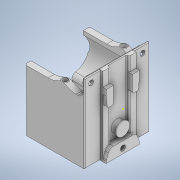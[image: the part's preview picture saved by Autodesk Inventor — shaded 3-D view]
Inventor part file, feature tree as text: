
AUTODESK INVENTOR PART (.ipt)
format: ipt  version: 2022 (Build 260153000, 153)  size: 863,232 bytes
history: native  units: mm
features: reference x27, sketch x24, extrude x22, projected_geometry x19, fillet x13, other x10, chamfer x1
ambient origin geometry x8: Origin, YZ Plane, XZ Plane, XY Plane, X Axis, Y Axis, Z Axis, Center Point
bodies: Body1 (feature_tree)
feature tree (116):
  other  "Твердое тело1"
  extrude  "Выдавливание1"  Depth=34.5mm TaperAngle=0.0deg
  extrude  "Выдавливание2"  Depth=0.5mm
  extrude  "Выдавливание3"  Depth=0.3mm
  extrude  "Выдавливание4"  Depth=5.0mm
  extrude  "Выдавливание5"  Depth=5.0mm
  extrude  "Выдавливание6"  Depth=5.0mm
  extrude  "Выдавливание8"  Depth=15.0mm
  extrude  "Выдавливание9"  Depth=15.0mm
  chamfer  "Фаска1"  Distance=15.0mm
  fillet  "Сопряжение1"  Radius=1.7mm
  extrude  "Выдавливание11"  Depth=2.0mm TaperAngle=0.0deg
  fillet  "Сопряжение4"  Radius=0.8mm
  fillet  "Сопряжение5"  Radius=4.7mm
  sketch  "Эскиз15"
  extrude  "Выдавливание12"  Depth=0.4mm
  sketch  "Эскиз17"
  extrude  "Выдавливание13"  Depth=0.4mm
  extrude  "Выдавливание18"  Depth=200.0mm TaperAngle=0.0deg
  extrude  "Выдавливание19"  Depth=0.5mm TaperAngle=0.0deg
  extrude  "Выдавливание20"  Depth=2.3mm TaperAngle=0.0deg
  extrude  "Выдавливание21"  Depth=10.0mm
  fillet  "Сопряжение13"  Radius=10.0mm
  fillet  "Сопряжение14"  Radius=3.0mm
  fillet  "Сопряжение15"  Radius=4.0mm
  extrude  "Выдавливание22"  Depth=3.0mm
  fillet  "Сопряжение16"  Radius=4.0mm
  extrude  "Выдавливание23"  Depth=2.3mm TaperAngle=0.0deg
  extrude  "Выдавливание24"  Depth=2.3mm TaperAngle=45.0deg
  fillet  "Сопряжение17"  Radius=10.0mm
  extrude  "Выдавливание25"  Depth=30.0mm
  fillet  "Сопряжение19"  Radius=0.8mm
  extrude  "Выдавливание26"  Depth=0.15mm
  fillet  "Сопряжение20"  Radius=3.0mm
  extrude  "Выдавливание27"  Depth=50.0mm TaperAngle=0.0deg
  fillet  "Сопряжение21"  Radius=4.0mm
  fillet  "Сопряжение22"  Radius=4.0mm
  fillet  "Сопряжение23"  Radius=3.2mm
  extrude  "Выдавливание28"  Depth=8.0mm
  sketch  "Эскиз1"
  reference  "Ссылка1"
  reference  "Ссылка2"
  reference  "Ссылка3"
  reference  "Ссылка4"
  reference  "Ссылка5"
  reference  "Ссылка6"
  reference  "Ссылка7"
  reference  "Ссылка8"
  sketch  "Эскиз2"
  projected_geometry  "Спроецированная петля1"
  projected_geometry  "Спроецированная петля2"
  sketch  "Эскиз3"
  reference  "Ссылка9"
  reference  "Ссылка10"
  sketch  "Эскиз4"
  projected_geometry  "Спроецированная петля3"
  reference  "Ссылка11"
  reference  "Ссылка12"
  reference  "Ссылка13"
  reference  "Ссылка14"
  sketch  "Эскиз5"
  reference  "Ссылка15"
  reference  "Ссылка16"
  projected_geometry  "Спроецированная петля4"
  sketch  "Эскиз7"
  projected_geometry  "Спроецированная петля6"
  sketch  "Эскиз11"
  projected_geometry  "Спроецированная петля8"
  sketch  "Эскиз12"
  reference  "Ссылка27"
  sketch  "Эскиз14"
  sketch  "Эскиз16"
  reference  "Ссылка29"
  projected_geometry  "Спроецированная петля10"
  projected_geometry  "Спроецированная петля11"
  projected_geometry  "Спроецированная петля12"
  reference  "Ссылка30"
  reference  "Ссылка31"
  sketch  "Эскиз18"
  projected_geometry  "Спроецированная петля14"
  sketch  "Эскиз23"
  projected_geometry  "Спроецированная петля23"
  sketch  "Эскиз24"
  projected_geometry  "Спроецированная петля24"
  sketch  "Эскиз25"
  sketch  "Эскиз26"
  sketch  "Эскиз27"
  projected_geometry  "Спроецированная петля25"
  sketch  "Эскиз28"
  sketch  "Эскиз29"
  sketch  "Эскиз30"
  reference  "Ссылка32"
  projected_geometry  "Спроецированная петля26"
  projected_geometry  "Спроецированная петля27"
  reference  "Ссылка33"
  projected_geometry  "Спроецированная петля28"
  sketch  "Эскиз31"
  projected_geometry  "Спроецированная петля29"
  projected_geometry  "Спроецированная петля30"
  reference  "Ссылка34"
  reference  "Ссылка35"
  sketch  "Эскиз32"
  reference  "Ссылка36"
  reference  "Ссылка37"
  reference  "Ссылка38"
  sketch  "Эскиз33"
  projected_geometry  "Спроецированная петля31"
  other  "<userpath>\OneDrive\Документы\Git\MZCAT_battery\FastBattery.iam"
  other  "FastBattery.iam"
  other  "plan:1"
  other  "BMS_board:1"
  other  "metal_body:1"
  other  "metal_cap:1"
  other  "<userpath>\Documents\Git\MZCAT_2024_construction\MZCAT_battery\FastBattery2.iam"
  other  "FastBattery2.iam"
  other  "metal_body_fixed:1"
